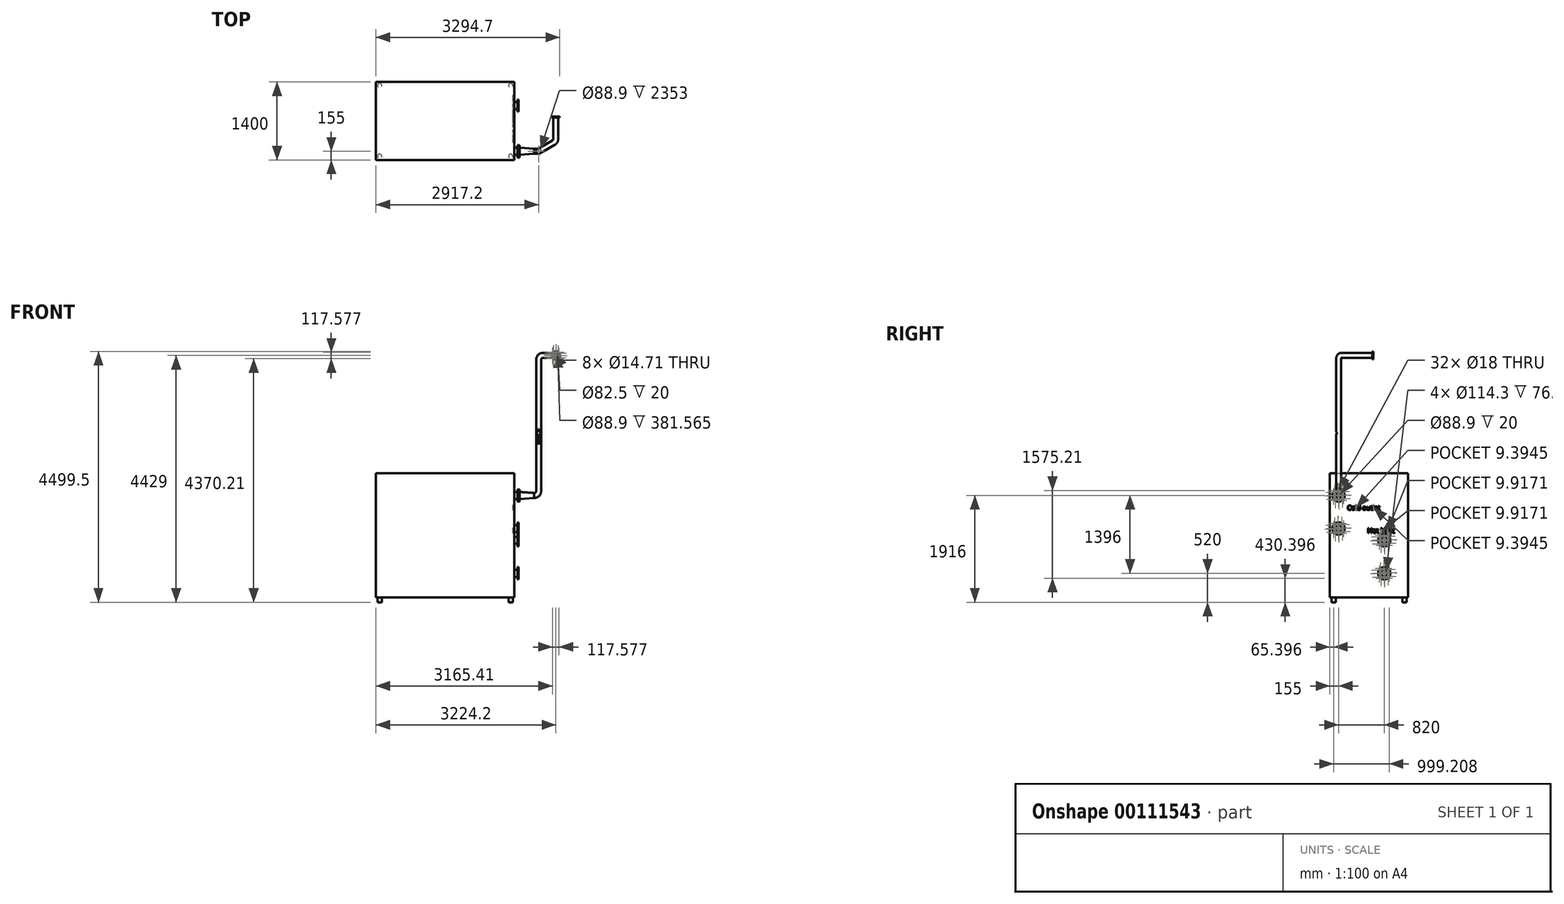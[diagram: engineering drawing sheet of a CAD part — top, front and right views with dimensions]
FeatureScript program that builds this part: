
annotation { "Feature Type Name" : "Feature", "Feature Type Description" : "" }
export const myFeature = defineFeature(function(context is Context, id is Id, definition is map)
    precondition{}
    {
        {
            var Q0;
            Q0=qCreatedBy(makeId("Top.planeOp"),FACE);
            var sketch = newSketch(context, id + "F0", { "sketchPlane" : qUnion([Q0])});
            skLineSegment(sketch, "E0.bottom", {"start": v(0, 0) * mm, "end": v(2481, 0) * mm});
            skLineSegment(sketch, "E0.top", {"start": v(0, 1400) * mm, "end": v(2481, 1400) * mm});
            skLineSegment(sketch, "E0.left", {"start": v(0, 0) * mm, "end": v(0, 1400) * mm});
            skLineSegment(sketch, "E0.right", {"start": v(2481, 0) * mm, "end": v(2481, 1400) * mm});
            skSolve(sketch);
        }
        {
            var Q0;
            Q0=qSketchRegion(id+"F0",true);
            extrude(context, id + "F1", {"entities" : qUnion([Q0]), "depth" : (2228 + 90) * mm});
        }
        {
            var Q0;
            Q0=makeQuery(id+"F1.opExtrude","SWEPT_FACE",FACE,{"disambiguationData":[OSD([sQuery(id+"F0.wireOp",EDGE,"E0.right")])]});
            var sketch = newSketch(context, id + "F2", { "sketchPlane" : qUnion([Q0])});
            skCircle(sketch, "E1", {"center": v(155, 1916) * mm, "radius": 57.15 * mm});
            skCircle(sketch, "E2", {"center": v(155, 1916) * mm, "radius": 62.15 * mm});
            skCircle(sketch, "E3", {"center": v(155, 1916) * mm, "radius": 110 * mm});
            skCircle(sketch, "E4", {"center": v(155, 1916) * mm, "radius": 90 * mm, "construction": true});
            skCircle(sketch, "E5", {"center": v(163.43, 1826.4) * mm, "radius": 9 * mm});
            skCircle(sketch, "E6.1.0", {"center": v(224.32, 1858.6) * mm, "radius": 9 * mm});
            skCircle(sketch, "E6.2.0", {"center": v(244.6, 1924.43) * mm, "radius": 9 * mm});
            skCircle(sketch, "E6.3.0", {"center": v(212.4, 1985.32) * mm, "radius": 9 * mm});
            skCircle(sketch, "E6.4.0", {"center": v(146.57, 2005.6) * mm, "radius": 9 * mm});
            skCircle(sketch, "E6.5.0", {"center": v(85.68, 1973.4) * mm, "radius": 9 * mm});
            skCircle(sketch, "E6.6.0", {"center": v(65.4, 1907.57) * mm, "radius": 9 * mm});
            skCircle(sketch, "E6.7.0", {"center": v(97.6, 1846.68) * mm, "radius": 9 * mm});
            skPoint(sketch, "E7.0.1.2", {"position": v(155, 1323) * mm});
            skCircle(sketch, "E7.0.1.4", {"center": v(155, 1323) * mm, "radius": 57.15 * mm});
            skCircle(sketch, "E7.0.1.5", {"center": v(155, 1323) * mm, "radius": 62.15 * mm});
            skCircle(sketch, "E7.0.1.6", {"center": v(155, 1323) * mm, "radius": 110 * mm});
            skCircle(sketch, "E7.0.1.7", {"center": v(155, 1323) * mm, "radius": 90 * mm, "construction": true});
            skCircle(sketch, "E7.0.1.13", {"center": v(97.6, 1253.68) * mm, "radius": 9 * mm});
            skCircle(sketch, "E7.0.1.15", {"center": v(244.6, 1331.43) * mm, "radius": 9 * mm});
            skCircle(sketch, "E7.0.1.16", {"center": v(212.4, 1392.32) * mm, "radius": 9 * mm});
            skCircle(sketch, "E7.0.1.17", {"center": v(146.57, 1412.6) * mm, "radius": 9 * mm});
            skCircle(sketch, "E7.0.1.18", {"center": v(163.43, 1233.4) * mm, "radius": 9 * mm});
            skCircle(sketch, "E7.0.1.19", {"center": v(85.68, 1380.4) * mm, "radius": 9 * mm});
            skCircle(sketch, "E7.0.1.20", {"center": v(65.4, 1314.57) * mm, "radius": 9 * mm});
            skCircle(sketch, "E7.0.1.21", {"center": v(224.32, 1265.6) * mm, "radius": 9 * mm});
            skLineSegment(sketch, "E7.direction1", {"start": v(97.6, 1846.68) * mm, "end": v(122.6, 1846.68) * mm, "construction": true});
            skLineSegment(sketch, "E7.direction2", {"start": v(97.6, 1846.68) * mm, "end": v(97.6, 1259.36) * mm, "construction": true});
            skSolve(sketch);
        }
        {
            var Q0;
            Q0=makeQuery(id+"F2.imprint","IMPRINT",FACE,{"disambiguationData":[TD([[makeQuery(id+"F2.imprint","IMPRINT",EDGE,{"derivedFrom":sQuery(id+"F2.wireOp",EDGE,"E1")}),-1.0]])]});
            var Q1;
            Q1=makeQuery(id+"F2.imprint","IMPRINT",FACE,{"disambiguationData":[TD([[makeQuery(id+"F2.imprint","IMPRINT",EDGE,{"derivedFrom":sQuery(id+"F2.wireOp",EDGE,"E7.0.1.4")}),-1.0]])]});
            extrude(context, id + "F3", {"entities" : qUnion([Q0, Q1]), "depth" : (76.2 - 22) * mm});
        }
        {
            var Q0;
            Q0=makeQuery(id+"F2.imprint","IMPRINT",FACE,{"disambiguationData":[TD([[makeQuery(id+"F2.imprint","IMPRINT",EDGE,{"derivedFrom":sQuery(id+"F2.wireOp",EDGE,"E7.0.1.4")}),-1.0]])]});
            var Q1;
            Q1=makeQuery(id+"F2.imprint","IMPRINT",FACE,{"disambiguationData":[TD([[makeQuery(id+"F2.imprint","IMPRINT",EDGE,{"derivedFrom":sQuery(id+"F2.wireOp",EDGE,"E7.0.1.5")}),-1.0]])]});
            var Q2;
            Q2=makeQuery(id+"F2.imprint","IMPRINT",FACE,{"disambiguationData":[TD([[makeQuery(id+"F2.imprint","IMPRINT",EDGE,{"derivedFrom":sQuery(id+"F2.wireOp",EDGE,"E1")}),-1.0]])]});
            var Q3;
            Q3=makeQuery(id+"F2.imprint","IMPRINT",FACE,{"disambiguationData":[TD([[makeQuery(id+"F2.imprint","IMPRINT",EDGE,{"derivedFrom":sQuery(id+"F2.wireOp",EDGE,"E2")}),-1.0]])]});
            var Q4;
            Q4=makeQuery(id+"F3.opExtrude","CAP_FACE",FACE,{"disambiguationData":[OSD([sQuery(id+"F2.wireOp",EDGE,"E7.0.1.4"),sQuery(id+"F2.wireOp",EDGE,"E7.0.1.5")])],"isStart":false});
            extrude(context, id + "F4", {"entities" : qUnion([Q0, Q1, Q2, Q3]), "operationType" : NewBodyOperationType.ADD, "depth" : 76.2 * mm, "hasSecondDirection" : true, "secondDirectionBound" : SecondDirectionBoundingType.UP_TO_SURFACE, "secondDirectionOppositeDirection" : false, "secondDirectionBoundEntityFace" : qUnion([Q4]), "secondDirectionDepth" : 104.68 * mm});
        }
        {
            var Q0;
            Q0=makeQuery(id+"F3.opExtrude","SWEPT_BODY",BODY,{"disambiguationData":[OSD([sQuery(id+"F2.wireOp",EDGE,"E1"),sQuery(id+"F2.wireOp",EDGE,"E2")])]});
            var Q1;
            Q1=makeQuery(id+"F3.opExtrude","SWEPT_BODY",BODY,{"disambiguationData":[OSD([sQuery(id+"F2.wireOp",EDGE,"E7.0.1.4"),sQuery(id+"F2.wireOp",EDGE,"E7.0.1.5")])]});
            transform(context, id + "F5", {"entities" : qUnion([Q0, Q1]), "transformType" : TransformType.TRANSLATION_3D, "dx" : 0 * mm, "dy" : (975 - 155) * mm, "dz" : (430 - 1233) * mm, "makeCopy" : true});
        }
        {
            var Q0;
            Q0=makeQuery(id+"F1.opExtrude","SWEPT_BODY",BODY,{"disambiguationData":[OSD([sQuery(id+"F0.wireOp",EDGE,"E0.bottom"),sQuery(id+"F0.wireOp",EDGE,"E0.top"),sQuery(id+"F0.wireOp",EDGE,"E0.left"),sQuery(id+"F0.wireOp",EDGE,"E0.right")])]});
            var Q1;
            Q1=makeQuery(id+"F3.opExtrude","SWEPT_BODY",BODY,{"disambiguationData":[OSD([sQuery(id+"F2.wireOp",EDGE,"E1"),sQuery(id+"F2.wireOp",EDGE,"E2")])]});
            var Q2;
            Q2=makeQuery(id+"F3.opExtrude","SWEPT_BODY",BODY,{"disambiguationData":[OSD([sQuery(id+"F2.wireOp",EDGE,"E7.0.1.4"),sQuery(id+"F2.wireOp",EDGE,"E7.0.1.5")])]});
            var Q3;
            Q3=makeQuery(id+"F5.opPattern","COPY",BODY,{"derivedFrom":makeQuery(id+"F3.opExtrude","SWEPT_BODY",BODY,{"disambiguationData":[OSD([sQuery(id+"F2.wireOp",EDGE,"E7.0.1.4"),sQuery(id+"F2.wireOp",EDGE,"E7.0.1.5")])]}),"instanceName":"1"});
            var Q4;
            Q4=makeQuery(id+"F5.opPattern","COPY",BODY,{"derivedFrom":makeQuery(id+"F3.opExtrude","SWEPT_BODY",BODY,{"disambiguationData":[OSD([sQuery(id+"F2.wireOp",EDGE,"E1"),sQuery(id+"F2.wireOp",EDGE,"E2")])]}),"instanceName":"1"});
            booleanBodies(context, id + "F6", {"operationType" : BooleanOperationType.UNION, "tools" : qUnion([Q0, Q1, Q2, Q3, Q4])});
        }
        {
            var Q0;
            Q0=makeQuery(id+"F2.imprint","IMPRINT",FACE,{"disambiguationData":[TD([[makeQuery(id+"F2.imprint","IMPRINT",EDGE,{"derivedFrom":sQuery(id+"F2.wireOp",EDGE,"E3")}),-1.0]])]});
            var sketch = newSketch(context, id + "F7", { "sketchPlane" : qUnion([Q0])});
            skText(sketch, "E8", { "text": "Hot inlet", "fontName": "OpenSans-Regular.ttf"});
            skText(sketch, "E9", { "text": "Cold outlet\n", "fontName": "OpenSans-Regular.ttf"});
            const initialGuessF7  = {"E8": [0.67256, 1.24268, 1, 0, 0.08805], "E9": [0.3111, 1.65511, 1, 0, 0.08341]};
            skSetInitialGuess(sketch, initialGuessF7);
            skSolve(sketch);
        }
        {
            var Q0;
            Q0=qSketchRegion(id+"F7",true);
            extrude(context, id + "F8", {"entities" : qUnion([Q0]), "operationType" : NewBodyOperationType.REMOVE, "oppositeDirection" : true, "depth" : 25 * mm});
        }
        {
            var Q0;
            Q0=sQuery(id+"F2.wireOp",VERTEX,"E1.center");
            var Q1;
            Q1=qCreatedBy(makeId("Front.planeOp"),FACE);
            cPlane(context, id + "F9", {"entities" : qUnion([Q0, Q1]), "cplaneType" : CPlaneType.PLANE_POINT, "offset" : 150 * mm, "width" : 150 * mm, "height" : 150 * mm});
        }
        {
            var Q0;
            Q0=qCreatedBy(id+"F9.planeOp",FACE);
            var sketch = newSketch(context, id + "F10", { "sketchPlane" : qUnion([Q0])});
            skLineSegment(sketch, "E10.0", {"start": v(2557.2, 1973.15) * mm, "end": v(2557.2, 1858.85) * mm});
            skPoint(sketch, "E11", {"position": v(2557.2, 1916) * mm});
            skLineSegment(sketch, "E12", {"start": v(2557.2, 1916) * mm, "end": v(2837.2, 1916) * mm});
            skLineSegment(sketch, "E13", {"start": v(2917.2, 1996) * mm, "end": v(2917.2, 4349) * mm, "construction": true});
            skLineSegment(sketch, "E14", {"start": v(2997.2, 4429) * mm, "end": v(4002.78, 4429) * mm, "construction": true});
            skPoint(sketch, "E15.visualSharp", {"position": v(2917.2, 4429) * mm});
            skArc(sketch, "E15.filletArc", {"start": v(2997.2, 4429) * mm, "mid": v(2940.63, 4405.57) * mm, "end": v(2917.2, 4349) * mm, "construction": true});
            skPoint(sketch, "E16.visualSharp", {"position": v(2917.2, 1916) * mm});
            skArc(sketch, "E16.filletArc", {"start": v(2837.2, 1916) * mm, "mid": v(2893.77, 1939.43) * mm, "end": v(2917.2, 1996) * mm});
            skLineSegment(sketch, "E17", {"start": v(2917.2, 2846.37) * mm, "end": v(2898.2, 2846.37) * mm});
            skLineSegment(sketch, "E18", {"start": v(2898.2, 2846.37) * mm, "end": v(2898.2, 3020.37) * mm});
            skLineSegment(sketch, "E19", {"start": v(2898.2, 3020.37) * mm, "end": v(2878.2, 3020.37) * mm});
            skLineSegment(sketch, "E20", {"start": v(2878.2, 3020.37) * mm, "end": v(2917.2, 3112.37) * mm});
            skLineSegment(sketch, "E21.MirrorCS", {"start": v(2956.2, 3020.37) * mm, "end": v(2917.2, 3112.37) * mm});
            skLineSegment(sketch, "E22.MirrorCS", {"start": v(2936.2, 2846.37) * mm, "end": v(2936.2, 3020.37) * mm});
            skLineSegment(sketch, "E23.MirrorCS", {"start": v(2936.2, 3020.37) * mm, "end": v(2956.2, 3020.37) * mm});
            skLineSegment(sketch, "E24.MirrorCS", {"start": v(2917.2, 2846.37) * mm, "end": v(2936.2, 2846.37) * mm});
            skLineSegment(sketch, "E25", {"start": v(2917.2, 1996) * mm, "end": v(2917.2, 2492.37) * mm});
            skSolve(sketch);
        }
        {
            var Q0;
            Q0=sQuery(id+"F10.wireOp",VERTEX,"E14.end");
            var Q1;
            Q1=qCreatedBy(makeId("Top.planeOp"),FACE);
            cPlane(context, id + "F11", {"entities" : qUnion([Q0, Q1]), "cplaneType" : CPlaneType.PLANE_POINT, "offset" : 150 * mm, "width" : 150 * mm, "height" : 150 * mm});
        }
        {
            var Q0;
            Q0=makeQuery(id+"F4.opExtrude","CAP_FACE",FACE,{"disambiguationData":[OSD([sQuery(id+"F2.wireOp",EDGE,"E1"),sQuery(id+"F2.wireOp",EDGE,"E3"),sQuery(id+"F2.wireOp",EDGE,"E5"),sQuery(id+"F2.wireOp",EDGE,"E6.1.0"),sQuery(id+"F2.wireOp",EDGE,"E6.2.0"),sQuery(id+"F2.wireOp",EDGE,"E6.3.0"),sQuery(id+"F2.wireOp",EDGE,"E6.4.0"),sQuery(id+"F2.wireOp",EDGE,"E6.5.0"),sQuery(id+"F2.wireOp",EDGE,"E6.6.0"),sQuery(id+"F2.wireOp",EDGE,"E6.7.0")])],"isStart":false});
            var sketch = newSketch(context, id + "F12", { "sketchPlane" : qUnion([Q0])});
            skCircle(sketch, "E26", {"center": v(155, 1916) * mm, "radius": 45.25 * mm});
            skCircle(sketch, "E27", {"center": v(155, 1916) * mm, "radius": 44.45 * mm});
            skCircle(sketch, "E28.0", {"center": v(155, 1916) * mm, "radius": 110 * mm});
            skCircle(sketch, "E28.1", {"center": v(85.68, 1973.4) * mm, "radius": 9 * mm});
            skCircle(sketch, "E28.2", {"center": v(65.4, 1907.57) * mm, "radius": 9 * mm});
            skCircle(sketch, "E28.3", {"center": v(97.6, 1846.68) * mm, "radius": 9 * mm});
            skCircle(sketch, "E28.4", {"center": v(163.43, 1826.4) * mm, "radius": 9 * mm});
            skCircle(sketch, "E28.5", {"center": v(224.32, 1858.6) * mm, "radius": 9 * mm});
            skCircle(sketch, "E28.6", {"center": v(244.6, 1924.43) * mm, "radius": 9 * mm});
            skCircle(sketch, "E28.7", {"center": v(212.4, 1985.32) * mm, "radius": 9 * mm});
            skCircle(sketch, "E28.8", {"center": v(146.57, 2005.6) * mm, "radius": 9 * mm});
            skSolve(sketch);
        }
        {
            var Q0;
            Q0=qCreatedBy(id+"F11.planeOp",FACE);
            var sketch = newSketch(context, id + "F13", { "sketchPlane" : qUnion([Q0])});
            skPoint(sketch, "E29.0", {"position": v(4002.78, 155) * mm});
            skLineSegment(sketch, "E30", {"start": v(4002.78, 155) * mm, "end": v(4016.77, 155) * mm, "construction": true});
            skLineSegment(sketch, "E31", {"start": v(4662.92, 835.27) * mm, "end": v(4662.92, 928.63) * mm, "construction": true});
            skPoint(sketch, "E32.visualSharp", {"position": v(4662.92, 155) * mm});
            skPoint(sketch, "E33.0", {"position": v(2917.2, 155) * mm});
            skLineSegment(sketch, "E34", {"start": v(3478.84, 355.73) * mm, "end": v(4609.84, 759.93) * mm, "construction": true});
            skArc(sketch, "E35.filletArc", {"start": v(4609.84, 759.93) * mm, "mid": v(4648.31, 789.2) * mm, "end": v(4662.92, 835.27) * mm, "construction": true});
            skPoint(sketch, "E36", {"position": v(3478.84, 355.73) * mm});
            skSolve(sketch);
        }
        {
            var Q0;
            Q0=sQuery(id+"F10.wireOp",VERTEX,"E15.visualSharp");
            var Q1;
            Q1=sQuery(id+"F10.wireOp",VERTEX,"E15.filletArc.end");
            var Q2;
            Q2=sQuery(id+"F13.wireOp",VERTEX,"E36");
            cPlane(context, id + "F14", {"entities" : qUnion([Q0, Q1, Q2]), "cplaneType" : CPlaneType.THREE_POINT, "offset" : 150 * mm, "width" : 150 * mm, "height" : 150 * mm});
        }
        {
            var Q0;
            Q0=sQuery(id+"F10.wireOp",EDGE,"E12");
            var Q1;
            Q1=sQuery(id+"F10.wireOp",VERTEX,"E16.visualSharp");
            cPlane(context, id + "F15", {"entities" : qUnion([Q0, Q1]), "cplaneType" : CPlaneType.LINE_POINT, "offset" : 150 * mm, "width" : 150 * mm, "height" : 150 * mm});
        }
        {
            var Q0;
            Q0=qCreatedBy(id+"F15.planeOp",FACE);
            var sketch = newSketch(context, id + "F16", { "sketchPlane" : qUnion([Q0])});
            skLineSegment(sketch, "E37.0", {"start": v(155, 2492.37) * mm, "end": v(155, 4349) * mm});
            skLineSegment(sketch, "E38", {"start": v(155, 4349) * mm, "end": v(155, 4349) * mm});
            skLineSegment(sketch, "E39", {"start": v(235, 4429) * mm, "end": v(252.39, 4429) * mm, "construction": true});
            skPoint(sketch, "E40.visualSharp", {"position": v(155, 4429) * mm});
            skArc(sketch, "E40.filletArc", {"start": v(235, 4429) * mm, "mid": v(178.43, 4405.57) * mm, "end": v(155, 4349) * mm, "construction": true});
            skPoint(sketch, "E41.0", {"position": v(155, 2492.37) * mm});
            skPoint(sketch, "E42.orphan", {"position": v(155, 1996) * mm});
            skSolve(sketch);
        }
        {
            var Q0;
            Q0=sQuery(id+"F16.wireOp",EDGE,"E37.0");
            cPlane(context, id + "F17", {"entities" : qUnion([Q0]), "cplaneType" : CPlaneType.LINE_ANGLE, "offset" : 150 * mm, "angle" : 120 * degree, "width" : 150 * mm, "height" : 150 * mm});
        }
        {
            var Q0;
            Q0=qCreatedBy(id+"F17.planeOp",FACE);
            var sketch = newSketch(context, id + "F18", { "sketchPlane" : qUnion([Q0])});
            skPoint(sketch, "E43.0", {"position": v(-2603.87, 4429) * mm});
            skLineSegment(sketch, "E44.0", {"start": v(-2603.87, 2492.37) * mm, "end": v(-2603.87, 4349) * mm});
            skLineSegment(sketch, "E45", {"start": v(-2603.87, 4349) * mm, "end": v(-2603.87, 4349) * mm});
            skLineSegment(sketch, "E46", {"start": v(-2683.87, 4429) * mm, "end": v(-2686.37, 4429) * mm});
            skArc(sketch, "E47.filletArc", {"start": v(-2603.87, 4349) * mm, "mid": v(-2627.3, 4405.57) * mm, "end": v(-2683.87, 4429) * mm});
            skSolve(sketch);
        }
        {
            var Q0;
            Q0=qCreatedBy(id+"F11.planeOp",FACE);
            var sketch = newSketch(context, id + "F19", { "sketchPlane" : qUnion([Q0])});
            skPoint(sketch, "E48.0", {"position": v(2917.2, 252.39) * mm});
            skLineSegment(sketch, "E49", {"start": v(2917.2, 252.39) * mm, "end": v(2917.2, 447) * mm, "construction": true});
            skLineSegment(sketch, "E50", {"start": v(2997.2, 527) * mm, "end": v(3144.2, 527) * mm, "construction": true});
            skLineSegment(sketch, "E51", {"start": v(3224.2, 607) * mm, "end": v(3224.2, 780) * mm});
            skPoint(sketch, "E52.visualSharp", {"position": v(2917.2, 527) * mm});
            skArc(sketch, "E52.filletArc", {"start": v(2997.2, 527) * mm, "mid": v(2940.63, 503.57) * mm, "end": v(2917.2, 447) * mm, "construction": true});
            skPoint(sketch, "E53.visualSharp", {"position": v(3224.2, 527) * mm});
            skArc(sketch, "E53.filletArc", {"start": v(3144.2, 527) * mm, "mid": v(3200.77, 550.43) * mm, "end": v(3224.2, 607) * mm, "construction": true});
            skPoint(sketch, "E54.0", {"position": v(2988.64, 196.25) * mm});
            skLineSegment(sketch, "E55", {"start": v(2988.64, 196.25) * mm, "end": v(3184.2, 309.15) * mm});
            skLineSegment(sketch, "E56", {"start": v(3224.2, 378.43) * mm, "end": v(3224.2, 607) * mm});
            skPoint(sketch, "E57.visualSharp", {"position": v(3224.2, 332.25) * mm});
            skArc(sketch, "E57.filletArc", {"start": v(3184.2, 309.15) * mm, "mid": v(3213.48, 338.43) * mm, "end": v(3224.2, 378.43) * mm});
            skSolve(sketch);
        }
        {
            var Q0;
            Q0=makeQuery(id+"F12.imprint","IMPRINT",FACE,{"disambiguationData":[TD([[makeQuery(id+"F12.imprint","IMPRINT",EDGE,{"derivedFrom":sQuery(id+"F12.wireOp",EDGE,"E26")}),1.0]])]});
            var Q1;
            Q1=sQuery(id+"F10.wireOp",EDGE,"E12");
            var Q2;
            Q2=sQuery(id+"F10.wireOp",EDGE,"E16.filletArc");
            var Q3;
            Q3=sQuery(id+"F10.wireOp",EDGE,"E25");
            var Q4;
            Q4=sQuery(id+"F16.wireOp",EDGE,"E37.0");
            var Q5;
            Q5=sQuery(id+"F16.wireOp",EDGE,"E40.filletArc");
            var Q6;
            Q6=sQuery(id+"F16.wireOp",EDGE,"E39");
            var Q7;
            Q7=sQuery(id+"F18.wireOp",EDGE,"E47.filletArc");
            var Q8;
            Q8=sQuery(id+"F18.wireOp",EDGE,"E46");
            var Q9;
            Q9=sQuery(id+"F19.wireOp",EDGE,"E55");
            var Q10;
            Q10=sQuery(id+"F19.wireOp",EDGE,"E57.filletArc");
            var Q11;
            Q11=sQuery(id+"F19.wireOp",EDGE,"E56");
            var Q12;
            Q12=sQuery(id+"F19.wireOp",EDGE,"E51");
            sweep(context, id + "F20", {"profiles" : qUnion([Q0]), "path" : qUnion([Q1, Q2, Q3, Q4, Q5, Q6, Q7, Q8, Q9, Q10, Q11, Q12])});
        }
        {
            var Q0;
            Q0=makeQuery(id+"F10.imprint","IMPRINT",FACE,{"disambiguationData":[TD([[makeQuery(id+"F10.imprint","IMPRINT",EDGE,{"derivedFrom":sQuery(id+"F10.wireOp",EDGE,"E17")}),-1.0]])]});
            var Q1;
            Q1=makeQuery(id+"F20.opSweep","SWEPT_FACE",FACE,{"disambiguationData":[OSD([sQuery(id+"F10.wireOp",EDGE,"E25"),sQuery(id+"F12.wireOp",EDGE,"E26")])]});
            extrude(context, id + "F21", {"entities" : qUnion([Q0]), "operationType" : NewBodyOperationType.REMOVE, "endBound" : BoundingType.UP_TO_SURFACE, "endBoundEntityFace" : qUnion([Q1]), "depth" : 25 * mm});
        }
        {
            var Q0;
            Q0=makeQuery(id+"F12.imprint","IMPRINT",FACE,{"disambiguationData":[TD([[makeQuery(id+"F12.imprint","IMPRINT",EDGE,{"derivedFrom":sQuery(id+"F12.wireOp",EDGE,"5eb4fbdf-50e4-4599-8a57-953bda03fb07")}),1.0]])]});
            var Q1;
            {var subQ0=makeQuery(id+"F4.opExtrude","CAP_EDGE",EDGE,{"disambiguationData":[OSD([sQuery(id+"F2.wireOp",EDGE,"E6.5.0")])],"isStart":false});var subQ1=sQuery(id+"F12.wireOp",EDGE,"10598bff-0ce2-465f-aa84-94724ede3573.5.0");var subQ3=makeQuery(id+"F12.imprint","INTERSECT",VERTEX,{"disambiguationData":[OD(0.0)],"derivedFrom":[subQ0,subQ1]});Q1=makeQuery(id+"F12.imprint","IMPRINT",FACE,{"disambiguationData":[TD([[makeQuery(id+"F12.imprint","IMPRINT",EDGE,{"disambiguationData":[TD([[subQ3,1.0]])],"derivedFrom":subQ1}),-1.0]])]});}
            var Q2;
            {var subQ0=makeQuery(id+"F4.opExtrude","CAP_EDGE",EDGE,{"disambiguationData":[OSD([sQuery(id+"F2.wireOp",EDGE,"E6.6.0")])],"isStart":false});var subQ1=sQuery(id+"F12.wireOp",EDGE,"10598bff-0ce2-465f-aa84-94724ede3573.6.0");var subQ3=makeQuery(id+"F12.imprint","INTERSECT",VERTEX,{"disambiguationData":[OD(0.0)],"derivedFrom":[subQ0,subQ1]});Q2=makeQuery(id+"F12.imprint","IMPRINT",FACE,{"disambiguationData":[TD([[makeQuery(id+"F12.imprint","IMPRINT",EDGE,{"disambiguationData":[TD([[subQ3,1.0]])],"derivedFrom":subQ1}),-1.0]])]});}
            var Q3;
            {var subQ0=makeQuery(id+"F4.opExtrude","CAP_EDGE",EDGE,{"disambiguationData":[OSD([sQuery(id+"F2.wireOp",EDGE,"E6.7.0")])],"isStart":false});var subQ1=sQuery(id+"F12.wireOp",EDGE,"10598bff-0ce2-465f-aa84-94724ede3573.7.0");var subQ3=makeQuery(id+"F12.imprint","INTERSECT",VERTEX,{"disambiguationData":[OD(0.0)],"derivedFrom":[subQ0,subQ1]});Q3=makeQuery(id+"F12.imprint","IMPRINT",FACE,{"disambiguationData":[TD([[makeQuery(id+"F12.imprint","IMPRINT",EDGE,{"disambiguationData":[TD([[subQ3,-1.0]])],"derivedFrom":subQ1}),-1.0]])]});}
            var Q4;
            {var subQ0=makeQuery(id+"F4.opExtrude","CAP_EDGE",EDGE,{"disambiguationData":[OSD([sQuery(id+"F2.wireOp",EDGE,"E5")])],"isStart":false});var subQ1=sQuery(id+"F12.wireOp",EDGE,"f2602a40-a317-41e3-a5e0-55ea5d988d8e");var subQ3=makeQuery(id+"F12.imprint","INTERSECT",VERTEX,{"disambiguationData":[OD(0.0)],"derivedFrom":[subQ0,subQ1]});Q4=makeQuery(id+"F12.imprint","IMPRINT",FACE,{"disambiguationData":[TD([[makeQuery(id+"F12.imprint","IMPRINT",EDGE,{"disambiguationData":[TD([[subQ3,-1.0]])],"derivedFrom":subQ1}),-1.0]])]});}
            var Q5;
            {var subQ0=makeQuery(id+"F4.opExtrude","CAP_EDGE",EDGE,{"disambiguationData":[OSD([sQuery(id+"F2.wireOp",EDGE,"E6.1.0")])],"isStart":false});var subQ1=sQuery(id+"F12.wireOp",EDGE,"10598bff-0ce2-465f-aa84-94724ede3573.1.0");var subQ3=makeQuery(id+"F12.imprint","INTERSECT",VERTEX,{"disambiguationData":[OD(0.0)],"derivedFrom":[subQ0,subQ1]});Q5=makeQuery(id+"F12.imprint","IMPRINT",FACE,{"disambiguationData":[TD([[makeQuery(id+"F12.imprint","IMPRINT",EDGE,{"disambiguationData":[TD([[subQ3,-1.0]])],"derivedFrom":subQ1}),-1.0]])]});}
            var Q6;
            {var subQ0=makeQuery(id+"F4.opExtrude","CAP_EDGE",EDGE,{"disambiguationData":[OSD([sQuery(id+"F2.wireOp",EDGE,"E6.3.0")])],"isStart":false});var subQ1=sQuery(id+"F12.wireOp",EDGE,"10598bff-0ce2-465f-aa84-94724ede3573.3.0");var subQ3=makeQuery(id+"F12.imprint","INTERSECT",VERTEX,{"disambiguationData":[OD(0.0)],"derivedFrom":[subQ0,subQ1]});Q6=makeQuery(id+"F12.imprint","IMPRINT",FACE,{"disambiguationData":[TD([[makeQuery(id+"F12.imprint","IMPRINT",EDGE,{"disambiguationData":[TD([[subQ3,1.0]])],"derivedFrom":subQ1}),-1.0]])]});}
            var Q7;
            {var subQ0=makeQuery(id+"F4.opExtrude","CAP_EDGE",EDGE,{"disambiguationData":[OSD([sQuery(id+"F2.wireOp",EDGE,"E6.4.0")])],"isStart":false});var subQ1=sQuery(id+"F12.wireOp",EDGE,"10598bff-0ce2-465f-aa84-94724ede3573.4.0");var subQ3=makeQuery(id+"F12.imprint","INTERSECT",VERTEX,{"disambiguationData":[OD(0.0)],"derivedFrom":[subQ0,subQ1]});Q7=makeQuery(id+"F12.imprint","IMPRINT",FACE,{"disambiguationData":[TD([[makeQuery(id+"F12.imprint","IMPRINT",EDGE,{"disambiguationData":[TD([[subQ3,1.0]])],"derivedFrom":subQ1}),-1.0]])]});}
            var Q8;
            {var subQ0=makeQuery(id+"F4.opExtrude","CAP_EDGE",EDGE,{"disambiguationData":[OSD([sQuery(id+"F2.wireOp",EDGE,"E6.2.0")])],"isStart":false});var subQ1=sQuery(id+"F12.wireOp",EDGE,"10598bff-0ce2-465f-aa84-94724ede3573.2.0");var subQ3=makeQuery(id+"F12.imprint","INTERSECT",VERTEX,{"disambiguationData":[OD(0.0)],"derivedFrom":[subQ0,subQ1]});Q8=makeQuery(id+"F12.imprint","IMPRINT",FACE,{"disambiguationData":[TD([[makeQuery(id+"F12.imprint","IMPRINT",EDGE,{"disambiguationData":[TD([[subQ3,-1.0]])],"derivedFrom":subQ1}),-1.0]])]});}
            var Q9;
            Q9=makeQuery(id+"F12.imprint","IMPRINT",FACE,{"disambiguationData":[TD([[makeQuery(id+"F12.imprint","IMPRINT",EDGE,{"derivedFrom":sQuery(id+"F12.wireOp",EDGE,"E26")}),-1.0]])]});
            var Q10;
            Q10=makeQuery(id+"F12.imprint","IMPRINT",FACE,{"disambiguationData":[TD([[makeQuery(id+"F12.imprint","IMPRINT",EDGE,{"derivedFrom":sQuery(id+"F12.wireOp",EDGE,"E28.0")}),1.0]])]});
            extrude(context, id + "F22", {"entities" : qUnion([Q0, Q1, Q2, Q3, Q4, Q5, Q6, Q7, Q8, Q9, Q10]), "operationType" : NewBodyOperationType.ADD, "depth" : 20 * mm});
        }
        {
            var Q0;
            Q0=makeQuery(id+"F20.opSweep","CAP_FACE",FACE,{"disambiguationData":[OSD([sQuery(id+"F12.wireOp",EDGE,"E26"),sQuery(id+"F12.wireOp",EDGE,"E27"),sQuery(id+"F13.wireOp",VERTEX,"E31.end")])],"isStart":false});
            var sketch = newSketch(context, id + "F23", { "sketchPlane" : qUnion([Q0])});
            skCircle(sketch, "E58", {"center": v(-3224.2, 4429) * mm, "radius": 70.5 * mm});
            skCircle(sketch, "E59.7.0", {"center": v(-3219.2, 4370.21) * mm, "radius": 7.35 * mm});
            skCircle(sketch, "E60", {"center": v(-3224.2, 4429) * mm, "radius": 59 * mm, "construction": true});
            skCircle(sketch, "E59.6.0", {"center": v(-3179.1, 4390.96) * mm, "radius": 7.35 * mm});
            skLineSegment(sketch, "E59.anchor2", {"start": v(-3224.2, 4429) * mm, "end": v(-3219.2, 4370.21) * mm, "construction": true});
            skCircle(sketch, "E61", {"center": v(-3224.2, 4429) * mm, "radius": 41.25 * mm});
            skCircle(sketch, "E62", {"center": v(-3262.24, 4383.9) * mm, "radius": 7.35 * mm});
            skLineSegment(sketch, "E59.anchor1", {"start": v(-3224.2, 4429) * mm, "end": v(-3262.24, 4383.9) * mm, "construction": true});
            skCircle(sketch, "E59.5.0", {"center": v(-3165.41, 4434) * mm, "radius": 7.35 * mm});
            skCircle(sketch, "E59.1.0", {"center": v(-3282.99, 4424) * mm, "radius": 7.35 * mm});
            skCircle(sketch, "E59.4.0", {"center": v(-3186.16, 4474.1) * mm, "radius": 7.35 * mm});
            skCircle(sketch, "E59.2.0", {"center": v(-3269.3, 4467.04) * mm, "radius": 7.35 * mm});
            skCircle(sketch, "E59.3.0", {"center": v(-3229.2, 4487.79) * mm, "radius": 7.35 * mm});
            skSolve(sketch);
        }
        {
            var Q0;
            Q0=qSketchRegion(id+"F23",true);
            extrude(context, id + "F24", {"entities" : qUnion([Q0]), "operationType" : NewBodyOperationType.ADD, "oppositeDirection" : true, "depth" : 20 * mm});
        }
        {
            var Q0;
            Q0=sQuery(id+"F10.wireOp",EDGE,"E12");
            cPlane(context, id + "F25", {"entities" : qUnion([Q0]), "cplaneType" : CPlaneType.LINE_ANGLE, "offset" : 150 * mm, "angle" : 0 * degree, "width" : 150 * mm, "height" : 150 * mm});
        }
        {
            var Q0;
            Q0=makeQuery(id+"F1.opExtrude","CAP_FACE",FACE,{"disambiguationData":[OSD([sQuery(id+"F0.wireOp",EDGE,"E0.bottom"),sQuery(id+"F0.wireOp",EDGE,"E0.top"),sQuery(id+"F0.wireOp",EDGE,"E0.left"),sQuery(id+"F0.wireOp",EDGE,"E0.right")])],"isStart":true});
            var sketch = newSketch(context, id + "F26", { "sketchPlane" : qUnion([Q0])});
            skLineSegment(sketch, "E63", {"start": v(0, -700) * mm, "end": v(2481, -700) * mm, "construction": true});
            skLineSegment(sketch, "E64", {"start": v(1240.5, 0) * mm, "end": v(1240.5, -1400) * mm, "construction": true});
            skCircle(sketch, "E65", {"center": v(65.58, -65.07) * mm, "radius": 38.33 * mm});
            skCircle(sketch, "E66.MirrorC", {"center": v(2415.42, -65.07) * mm, "radius": 38.33 * mm});
            skCircle(sketch, "E67.MirrorC", {"center": v(65.58, -1334.93) * mm, "radius": 38.33 * mm});
            skCircle(sketch, "E68.MirrorC", {"center": v(2415.42, -1334.93) * mm, "radius": 38.33 * mm});
            skLineSegment(sketch, "E69.0", {"start": v(0, 0) * mm, "end": v(2481, 0) * mm});
            skLineSegment(sketch, "E69.1", {"start": v(0, 0) * mm, "end": v(0, -1400) * mm});
            skLineSegment(sketch, "E69.2", {"start": v(0, -1400) * mm, "end": v(2481, -1400) * mm});
            skPoint(sketch, "E69.3", {"position": v(2481, -866.86) * mm});
            skLineSegment(sketch, "E69.4", {"start": v(2481, 0) * mm, "end": v(2481, -1400) * mm});
            skSolve(sketch);
        }
        {
            var Q0;
            Q0=qSketchRegion(id+"F26",true);
            extrude(context, id + "F27", {"entities" : qUnion([Q0]), "operationType" : NewBodyOperationType.REMOVE, "oppositeDirection" : true, "depth" : 90 * mm});
        }
        {
            var Q0;
            Q0=qCreatedBy(id+"F25.planeOp",FACE);
            var sketch = newSketch(context, id + "F28", { "sketchPlane" : qUnion([Q0])});
            skLineSegment(sketch, "E70.0", {"start": v(-2557.2, 1916) * mm, "end": v(-2837.2, 1916) * mm});
            skLineSegment(sketch, "E71.1", {"start": v(-2577.2, 1806) * mm, "end": v(-2577.2, 2026) * mm});
            skPoint(sketch, "E72", {"position": v(-2577.2, 1979.38) * mm});
            skLineSegment(sketch, "E73.0", {"start": v(-2837.2, 1870.75) * mm, "end": v(-2837.2, 1961.25) * mm});
            skLineSegment(sketch, "E74", {"start": v(-2837.2, 1961.25) * mm, "end": v(-2577.2, 1979.38) * mm});
            skSolve(sketch);
        }
        {
            var Q0;
            Q0=qSketchRegion(id+"F28",true);
            var Q1;
            Q1=sQuery(id+"F28.wireOp",EDGE,"E70.0");
            revolve(context, id + "F29", {"operationType" : NewBodyOperationType.ADD, "entities" : qUnion([Q0]), "axis" : qUnion([Q1]), "revolveType" : RevolveType.FULL});
        }
    });
